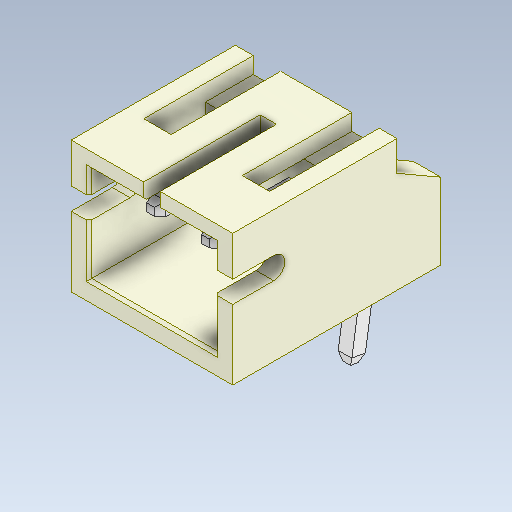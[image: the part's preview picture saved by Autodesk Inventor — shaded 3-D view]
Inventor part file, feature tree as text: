
AUTODESK INVENTOR PART (.ipt)
format: ipt  version: 2020 (Build 240168000, 168)  size: 188,928 bytes
history: native  units: mm
features: other x3, chamfer x3
ambient origin geometry x8: Origin, YZ Plane, XZ Plane, XY Plane, X Axis, Y Axis, Z Axis, Center Point
bodies: Body1 (feature_tree), Body2 (feature_tree), Body3 (feature_tree)
feature tree (6):
  other  "Твердое тело1"
  other  "Твердое тело2"
  other  "Твердое тело3"
  chamfer  "Chamfer3"  [1 undecoded]
  chamfer  "Chamfer2"  [1 undecoded]
  chamfer  "Chamfer1"  [1 undecoded]
note: 3 required parameter values undecoded (feature->parameter linkage not recoverable at this tier; creation-order binding heuristic only, values carry confidence <= 0.55)
